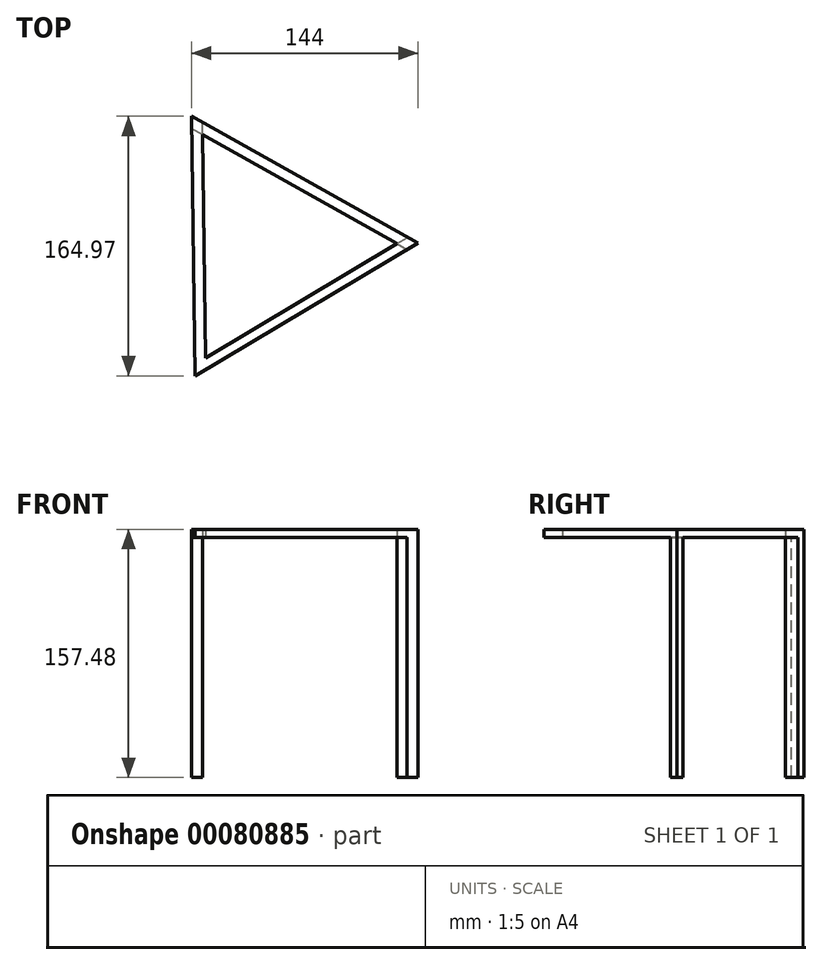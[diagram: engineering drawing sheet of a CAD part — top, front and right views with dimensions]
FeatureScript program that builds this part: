
annotation { "Feature Type Name" : "Feature", "Feature Type Description" : "" }
export const myFeature = defineFeature(function(context is Context, id is Id, definition is map)
    precondition{}
    {
        {
            var Q0;
            Q0=qCreatedBy(makeId("Top.planeOp"),FACE);
            var sketch = newSketch(context, id + "F0", { "sketchPlane" : qUnion([Q0])});
            skLineSegment(sketch, "E0.0", {"start": v(-48.76, 81.83) * mm, "end": v(95.24, 1.31) * mm});
            skLineSegment(sketch, "E0.1", {"start": v(95.24, 1.31) * mm, "end": v(-46.49, -83.14) * mm});
            skLineSegment(sketch, "E0.2", {"start": v(-46.49, -83.14) * mm, "end": v(-48.76, 81.83) * mm});
            skPoint(sketch, "E0.0.midPoint", {"position": v(23.24, 41.57) * mm});
            skLineSegment(sketch, "E1", {"start": v(81.89, 0.85) * mm, "end": v(-41.78, 70) * mm});
            skLineSegment(sketch, "E2", {"start": v(-41.78, 70) * mm, "end": v(-39.83, -71.67) * mm});
            skLineSegment(sketch, "E3", {"start": v(-39.83, -71.67) * mm, "end": v(81.89, 0.85) * mm});
            skSolve(sketch);
        }
        {
            var Q0;
            Q0=makeQuery(id+"F0.imprint","IMPRINT",FACE,{"disambiguationData":[TD([[makeQuery(id+"F0.imprint","IMPRINT",EDGE,{"derivedFrom":sQuery(id+"F0.wireOp",EDGE,"E0.0")}),-1.0]])]});
            extrude(context, id + "F1", {"entities" : qUnion([Q0]), "depth" : 5.08 * mm});
        }
        {
            var Q0;
            Q0=makeQuery(id+"F1.opExtrude","CAP_FACE",FACE,{"disambiguationData":[OSD([sQuery(id+"F0.wireOp",EDGE,"E0.0"),sQuery(id+"F0.wireOp",EDGE,"E0.1"),sQuery(id+"F0.wireOp",EDGE,"E0.2"),sQuery(id+"F0.wireOp",EDGE,"E1"),sQuery(id+"F0.wireOp",EDGE,"E2"),sQuery(id+"F0.wireOp",EDGE,"E3")])],"isStart":true});
            var sketch = newSketch(context, id + "F2", { "sketchPlane" : qUnion([Q0])});
            skLineSegment(sketch, "E4", {"start": v(-39.83, 71.67) * mm, "end": v(-46.59, 75.7) * mm});
            skLineSegment(sketch, "E5", {"start": v(-46.59, 75.7) * mm, "end": v(-39.83, 71.67) * mm});
            skLineSegment(sketch, "E6", {"start": v(-39.83, 71.67) * mm, "end": v(-39.83, 79.17) * mm});
            skLineSegment(sketch, "E7", {"start": v(-46.49, 83.14) * mm, "end": v(-46.59, 75.7) * mm});
            skLineSegment(sketch, "E8", {"start": v(-41.78, -70) * mm, "end": v(-48.65, -73.84) * mm});
            skLineSegment(sketch, "E9", {"start": v(-41.78, -70) * mm, "end": v(-41.78, -77.93) * mm});
            skLineSegment(sketch, "E10", {"start": v(-41.78, -77.93) * mm, "end": v(-48.76, -81.83) * mm});
            skLineSegment(sketch, "E11", {"start": v(-48.76, -81.83) * mm, "end": v(-48.65, -73.84) * mm});
            skLineSegment(sketch, "E12", {"start": v(81.89, -0.85) * mm, "end": v(88.75, -4.94) * mm});
            skLineSegment(sketch, "E13", {"start": v(88.75, -4.94) * mm, "end": v(95.24, -1.31) * mm});
            skLineSegment(sketch, "E14", {"start": v(81.89, -0.85) * mm, "end": v(88.25, 2.86) * mm});
            skLineSegment(sketch, "E15", {"start": v(88.25, 2.86) * mm, "end": v(95.24, -1.31) * mm});
            skSolve(sketch);
        }
        {
            var Q0;
            Q0 = qSketchRegion(id + "F2", true);
            var Q1;
            Q1=makeQuery(id+"F2.imprint","IMPRINT",FACE,{"disambiguationData":[TD([[makeQuery(id+"F2.imprint","IMPRINT",EDGE,{"derivedFrom":sQuery(id+"F2.wireOp",EDGE,"E5")}),1.0]])]});
            extrude(context, id + "F3", {"entities" : qUnion([Q0, Q1]), "operationType" : NewBodyOperationType.ADD, "depth" : 152.4 * mm});
        }
    });
